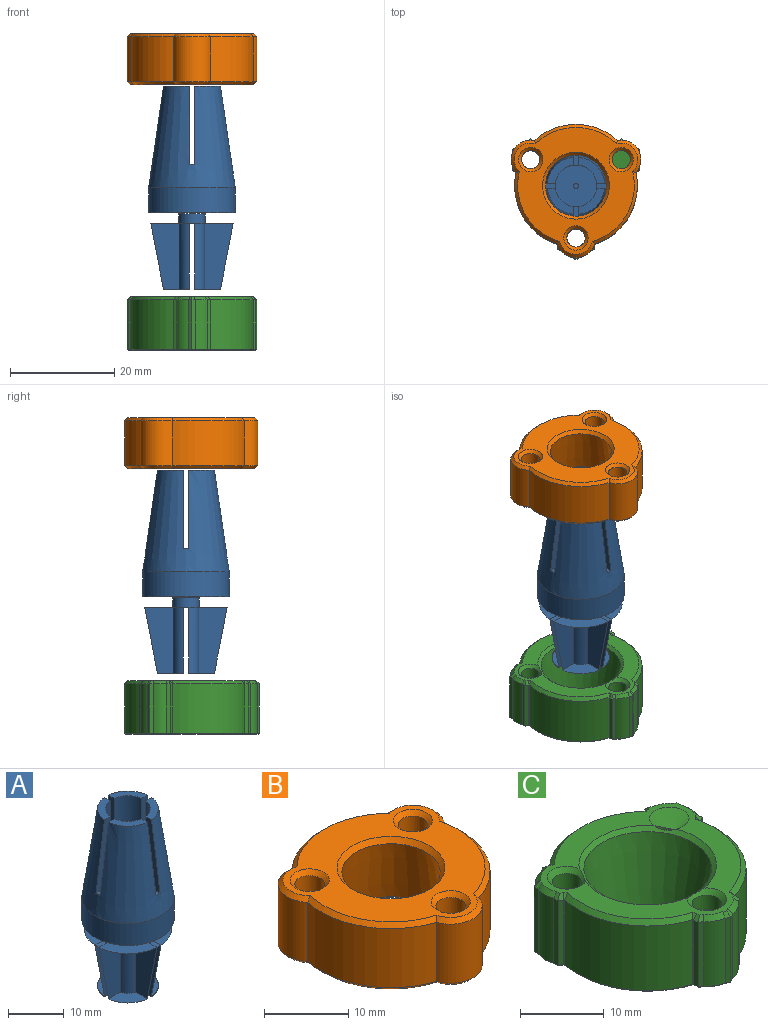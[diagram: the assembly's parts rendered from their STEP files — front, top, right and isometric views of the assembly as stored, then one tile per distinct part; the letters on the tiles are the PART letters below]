
ASSEMBLY  parts=3 mates=2
PART A: 40 faces, bbox 16.6x16.6x38.9 mm
  f0: plane 4.96x4.96mm, normal (0,0,-1), area 15.7mm2, adj f4,f5,f32,f38
  f1: plane 4.96x4.96mm, normal (0,0,-1), area 15.7mm2, adj f4,f5,f31,f35
  f2: plane 4.96x4.96mm, normal (0,0,-1), area 15.7mm2, adj f4,f5,f28,f37
  f3: plane 4.96x4.96mm, normal (0,0,-1), area 15.7mm2, adj f4,f5,f29,f34
  f4: cone r=8.3mm half-angle=10.9deg, axis (0,0,1), area 55.8mm2, adj f0,f1,f2,f3,f11,f28,f29,f30
  f5: cylinder r=2.5mm len=14.41mm, axis (0,0,-1), area 175.9mm2, adj f0,f1,f2,f3,f15,f28,f29,f30
  f6: cone r=5.48mm half-angle=8.2deg, axis (0,0,-1), area 789.9mm2, adj f7,f8,f9,f10,f11,f16,f17,f18
  f7: plane 4.96x4.96mm, normal (0,0,1), area 9.6mm2, adj f6,f12,f16,f25
  f8: plane 4.96x4.96mm, normal (0,0,1), area 9.6mm2, adj f6,f12,f17,f23
  f9: plane 4.96x4.96mm, normal (0,0,1), area 9.6mm2, adj f6,f12,f20,f26
  f10: plane 4.96x4.96mm, normal (0,0,1), area 9.6mm2, adj f6,f12,f19,f24
  f11: cylinder r=8.3mm len=16.6mm, axis (0,0,-1), area 249.6mm2, adj f4,f6
  f12: cylinder r=4mm len=19.47mm, axis (0,0,-1), area 429.1mm2, adj f7,f8,f9,f10,f13,f16,f17,f18
  f13: plane 8x8mm, normal (0,0,1), area 49.5mm2, adj f12,f14
  f14: cylinder r=0.5mm len=5mm, axis (0,0,-1), area 15.7mm2, adj f13,f15
  f15: plane 5x5mm, normal (0,0,-1), area 18.8mm2, adj f5,f14
  f16: plane 15.03x3.7mm, normal (0,1,0), area 38.7mm2, adj f6,f7,f12,f18
  f17: plane 15.03x3.7mm, normal (0,-1,0), area 38.7mm2, adj f6,f8,f12,f18
  f18: plane 3.69x1mm, normal (0,0,1), area 3.7mm2, adj f6,f12,f16,f17
  f19: plane 15.03x3.7mm, normal (0,-1,0), area 38.7mm2, adj f6,f10,f12,f21
  f20: plane 15.03x3.7mm, normal (0,1,0), area 38.7mm2, adj f6,f9,f12,f21
  f21: plane 3.69x1mm, normal (0,0,1), area 3.7mm2, adj f6,f12,f19,f20
  f22: plane 3.69x1mm, normal (0,0,1), area 3.7mm2, adj f6,f12,f23,f24
  f23: plane 15.03x3.7mm, normal (1,0,0), area 38.7mm2, adj f6,f8,f12,f22
  f24: plane 15.03x3.7mm, normal (-1,0,0), area 38.7mm2, adj f6,f10,f12,f22
  f25: plane 15.03x3.7mm, normal (1,0,0), area 38.7mm2, adj f6,f7,f12,f27
  f26: plane 15.03x3.7mm, normal (-1,0,0), area 38.7mm2, adj f6,f9,f12,f27
  f27: plane 3.69x1mm, normal (0,0,1), area 3.7mm2, adj f6,f12,f25,f26
  f28: plane 12.58x5.47mm, normal (-1,0,0), area 53mm2, adj f2,f4,f5,f30
  f29: plane 12.58x5.47mm, normal (1,0,0), area 53mm2, adj f3,f4,f5,f30
  f30: plane 5.45x1mm, normal (0,0,-1), area 5.4mm2, adj f4,f5,f28,f29
  f31: plane 12.58x5.47mm, normal (1,0,0), area 53mm2, adj f1,f4,f5,f33
  f32: plane 12.58x5.47mm, normal (-1,0,0), area 53mm2, adj f0,f4,f5,f33
  f33: plane 5.45x1mm, normal (0,0,-1), area 5.4mm2, adj f4,f5,f31,f32
  f34: plane 12.58x5.47mm, normal (0,1,0), area 53mm2, adj f3,f4,f5,f36
  f35: plane 12.58x5.47mm, normal (0,-1,0), area 53mm2, adj f1,f4,f5,f36
  f36: plane 5.45x1mm, normal (0,0,-1), area 5.4mm2, adj f4,f5,f34,f35
  f37: plane 12.58x5.47mm, normal (0,1,0), area 53mm2, adj f2,f4,f5,f39
  f38: plane 12.58x5.47mm, normal (0,-1,0), area 53mm2, adj f0,f4,f5,f39
  f39: plane 15.8x15.8mm, normal (0,0,-1), area 190.6mm2, adj f4,f5,f37,f38
PART B: 32 faces, bbox 24.8x25.5x9.7 mm
  f0: plane 24.34x23.67mm, normal (0,0,1), area 240.2mm2, adj f12,f13,f14,f15,f16,f17,f18,f19
  f1: cylinder r=11.75mm len=13.71mm, axis (0,0,-1), area 149.1mm2, adj f6,f10,f16,f26
  f2: cylinder r=11.75mm len=15.84mm, axis (0,0,-1), area 149.1mm2, adj f8,f10,f20,f30
  f3: plane 24.34x23.67mm, normal (0,0,-1), area 185.4mm2, adj f22,f23,f24,f25,f26,f27,f28,f29
  f4: cylinder r=11.75mm len=13.71mm, axis (0,0,-1), area 149.1mm2, adj f6,f8,f17,f27
  f5: cone r=7.14mm half-angle=8.2deg, axis (0,0,-1), area 351.4mm2, adj f21,f31
  f6: cylinder r=3.75mm len=8.58mm, axis (0,0,1), area 80.2mm2, adj f1,f4,f15,f25
  f7: cylinder r=1.75mm len=8.58mm, axis (0,0,1), area 94.3mm2, adj f14,f24
  f8: cylinder r=3.75mm len=8.58mm, axis (0,0,1), area 80.2mm2, adj f2,f4,f19,f29
  f9: cylinder r=1.75mm len=8.58mm, axis (0,0,1), area 94.3mm2, adj f13,f23
  f10: cylinder r=3.75mm len=8.58mm, axis (0,0,1), area 80.2mm2, adj f1,f2,f18,f28
  f11: cylinder r=1.75mm len=8.58mm, axis (0,0,1), area 94.3mm2, adj f12,f22
  f12: cone r=1.75mm half-angle=45deg, axis (0,0,1), area 10.5mm2, adj f0,f11
  f13: cone r=1.75mm half-angle=45deg, axis (0,0,1), area 10.5mm2, adj f0,f9
  f14: cone r=1.75mm half-angle=45deg, axis (0,0,1), area 10.5mm2, adj f0,f7
  f15: cone r=3.17mm half-angle=45deg, axis (0,0,-1), area 7.3mm2, adj f0,f6,f16,f17
  f16: cone r=11.75mm half-angle=45deg, axis (0,0,-1), area 14.1mm2, adj f0,f1,f15,f18
  f17: cone r=11.75mm half-angle=45deg, axis (0,0,-1), area 14.1mm2, adj f0,f4,f15,f19
  f18: cone r=3.17mm half-angle=45deg, axis (0,0,-1), area 7.3mm2, adj f0,f10,f16,f20
  f19: cone r=3.17mm half-angle=45deg, axis (0,0,-1), area 7.3mm2, adj f0,f8,f17,f20
  f20: cone r=11.75mm half-angle=45deg, axis (0,0,-1), area 14.1mm2, adj f0,f2,f18,f19
  f21: cone r=6.4mm half-angle=40.9deg, axis (0,0,1), area 33.6mm2, adj f0,f5
  f22: cone r=1.75mm half-angle=45deg, axis (0,0,-1), area 10.5mm2, adj f3,f11
  f23: cone r=1.75mm half-angle=45deg, axis (0,0,-1), area 10.5mm2, adj f3,f9
  f24: cone r=1.75mm half-angle=45deg, axis (0,0,-1), area 10.5mm2, adj f3,f7
  f25: cone r=3.17mm half-angle=45deg, axis (0,0,1), area 7.3mm2, adj f3,f6,f26,f27
  f26: cone r=11.17mm half-angle=45deg, axis (0,0,1), area 14.1mm2, adj f1,f3,f25,f28
  f27: cone r=11.17mm half-angle=45deg, axis (0,0,1), area 14.1mm2, adj f3,f4,f25,f29
  f28: cone r=3.17mm half-angle=45deg, axis (0,0,1), area 7.3mm2, adj f3,f10,f26,f30
  f29: cone r=3.17mm half-angle=45deg, axis (0,0,1), area 7.3mm2, adj f3,f8,f27,f30
  f30: cone r=11.17mm half-angle=45deg, axis (0,0,1), area 14.1mm2, adj f2,f3,f28,f29
  f31: cone r=7.07mm half-angle=49.1deg, axis (0,0,-1), area 35mm2, adj f3,f5
PART C: 155 faces, bbox 24.8x25.8x10.3 mm
  f0: cylinder r=1.75mm len=3.5mm, axis (0,0,-1), area 23.9mm2, adj f145,f152
  f1: cylinder r=1.75mm len=3.5mm, axis (0,0,-1), area 23.9mm2, adj f146,f154
  f2: cylinder r=1.75mm len=3.5mm, axis (0,0,-1), area 23.9mm2, adj f148,f150
  f3: plane 25.36x24.41mm, normal (0,0,-1), area 243.8mm2, adj f60,f61,f62,f63,f64,f65,f66,f67
  f4: cylinder r=3.75mm len=9.47mm, axis (0,0,-1), area 25.2mm2, adj f40,f45,f83,f122
  f5: cylinder r=3.75mm len=9.47mm, axis (0,0,-1), area 1.1mm2, adj f13,f42,f95,f134
  f6: cylinder r=3.75mm len=9.47mm, axis (0,0,-1), area 25.2mm2, adj f41,f43,f89,f128
  f7: cylinder r=3.75mm len=9.47mm, axis (0,0,-1), area 25.2mm2, adj f34,f39,f104,f144
  f8: cylinder r=3.75mm len=9.47mm, axis (0,0,-1), area 1.1mm2, adj f14,f36,f92,f133
  f9: cylinder r=3.75mm len=9.47mm, axis (0,0,-1), area 25.2mm2, adj f35,f37,f98,f139
  f10: cylinder r=3.75mm len=9.47mm, axis (0,0,-1), area 1.1mm2, adj f15,f25,f73,f112
  f11: cylinder r=3.75mm len=9.47mm, axis (0,0,-1), area 25.2mm2, adj f23,f26,f76,f117
  f12: cylinder r=3.75mm len=9.47mm, axis (0,0,-1), area 25.2mm2, adj f21,f24,f82,f123
  f13: cylinder r=11.75mm len=13.71mm, axis (0,0,-1), area 164.5mm2, adj f5,f20,f97,f136
  f14: cylinder r=11.75mm len=13.71mm, axis (0,0,-1), area 164.5mm2, adj f8,f19,f90,f131
  f15: cylinder r=11.75mm len=15.84mm, axis (0,0,-1), area 164.5mm2, adj f10,f18,f75,f114
  f16: plane 24.5x23.61mm, normal (0,0,1), area 157.5mm2, adj f112,f113,f114,f115,f116,f117,f118,f119
  f17: cone r=5.74mm half-angle=10.9deg, axis (0,0,1), area 409.3mm2, adj f111,f147
  f18: cylinder r=3.75mm len=9.47mm, axis (0,0,-1), area 1.1mm2, adj f15,f44,f77,f116
  f19: cylinder r=3.75mm len=9.47mm, axis (0,0,-1), area 1.1mm2, adj f14,f22,f88,f129
  f20: cylinder r=3.75mm len=9.47mm, axis (0,0,-1), area 1.1mm2, adj f13,f38,f99,f138
  f21: plane 9.47x0.73mm, normal (1,0,0), area 6.9mm2, adj f12,f22,f84,f125
  f22: plane 9.47x0.63mm, normal (0.5,-0.87,0), area 6.9mm2, adj f19,f21,f86,f127
  f23: plane 9.47x0.63mm, normal (0.5,0.87,0), area 6.9mm2, adj f11,f24,f78,f119
  f24: plane 9.47x0.73mm, normal (1,0,0), area 6.9mm2, adj f12,f23,f80,f121
  f25: plane 9.47x0.63mm, normal (-0.5,0.87,0), area 6.9mm2, adj f10,f26,f72,f113
  f26: plane 9.47x0.63mm, normal (0.5,0.87,0), area 6.9mm2, adj f11,f25,f74,f115
  f27: plane 2.8x2.29mm, normal (0.5,-0.87,0), area 7.4mm2, adj f28,f32,f33,f110
  f28: plane 2.8x2.29mm, normal (-0.5,-0.87,0), area 7.4mm2, adj f27,f29,f33,f108
  f29: plane 3.23x2.29mm, normal (-1,0,0), area 7.4mm2, adj f28,f30,f33,f106
  f30: plane 2.8x2.29mm, normal (-0.5,0.87,0), area 7.4mm2, adj f29,f31,f33,f105
  f31: plane 2.8x2.29mm, normal (0.5,0.87,0), area 7.4mm2, adj f30,f32,f33,f107
  f32: plane 3.23x2.29mm, normal (1,0,0), area 7.4mm2, adj f27,f31,f33,f109
  f33: plane 6.47x5.6mm, normal (0,0,-1), area 7.5mm2, adj f27,f28,f29,f30,f31,f32,f153
  f34: plane 9.47x0.63mm, normal (-0.5,-0.87,0), area 6.9mm2, adj f7,f35,f102,f143
  f35: plane 9.47x0.63mm, normal (0.5,-0.87,0), area 6.9mm2, adj f9,f34,f100,f141
  f36: plane 9.47x0.73mm, normal (1,0,0), area 6.9mm2, adj f8,f37,f94,f135
  f37: plane 9.47x0.63mm, normal (0.5,-0.87,0), area 6.9mm2, adj f9,f36,f96,f137
  f38: plane 9.47x0.73mm, normal (-1,0,0), area 6.9mm2, adj f20,f39,f101,f140
  f39: plane 9.47x0.63mm, normal (-0.5,-0.87,0), area 6.9mm2, adj f7,f38,f103,f142
  f40: plane 9.47x0.63mm, normal (-0.5,0.87,0), area 6.9mm2, adj f4,f41,f85,f124
  f41: plane 9.47x0.73mm, normal (-1,0,0), area 6.9mm2, adj f6,f40,f87,f126
  f42: plane 9.47x0.63mm, normal (-0.5,-0.87,0), area 6.9mm2, adj f5,f43,f93,f132
  f43: plane 9.47x0.73mm, normal (-1,0,0), area 6.9mm2, adj f6,f42,f91,f130
  f44: plane 9.47x0.63mm, normal (0.5,0.87,0), area 6.9mm2, adj f18,f45,f79,f118
  f45: plane 9.47x0.63mm, normal (-0.5,0.87,0), area 6.9mm2, adj f4,f44,f81,f120
  f46: plane 2.8x2.29mm, normal (0.5,-0.87,0), area 7.4mm2, adj f47,f51,f52,f65
  f47: plane 2.8x2.29mm, normal (-0.5,-0.87,0), area 7.4mm2, adj f46,f48,f52,f63
  f48: plane 3.23x2.29mm, normal (-1,0,0), area 7.4mm2, adj f47,f49,f52,f61
  f49: plane 2.8x2.29mm, normal (-0.5,0.87,0), area 7.4mm2, adj f48,f50,f52,f60
  f50: plane 2.8x2.29mm, normal (0.5,0.87,0), area 7.4mm2, adj f49,f51,f52,f62
  f51: plane 3.23x2.29mm, normal (1,0,0), area 7.4mm2, adj f46,f50,f52,f64
  f52: plane 6.47x5.6mm, normal (0,0,-1), area 7.5mm2, adj f46,f47,f48,f49,f50,f51,f151
  f53: plane 2.8x2.29mm, normal (0.5,0.87,0), area 7.4mm2, adj f54,f58,f59,f71
  f54: plane 3.23x2.29mm, normal (1,0,0), area 7.4mm2, adj f53,f55,f59,f69
  f55: plane 2.8x2.29mm, normal (0.5,-0.87,0), area 7.4mm2, adj f54,f56,f59,f67
  f56: plane 2.8x2.29mm, normal (-0.5,-0.87,0), area 7.4mm2, adj f55,f57,f59,f66
  f57: plane 3.23x2.29mm, normal (-1,0,0), area 7.4mm2, adj f56,f58,f59,f68
  f58: plane 2.8x2.29mm, normal (-0.5,0.87,0), area 7.4mm2, adj f53,f57,f59,f70
  f59: plane 6.47x5.6mm, normal (0,0,-1), area 7.5mm2, adj f53,f54,f55,f56,f57,f58,f149
  f60: plane 3.01x1.86mm, normal (-0.35,0.61,-0.71), area 1mm2, adj f3,f49,f61,f62
  f61: plane 3.47x0.21mm, normal (-0.71,0,-0.71), area 1mm2, adj f3,f48,f60,f63
  f62: plane 3.01x1.86mm, normal (0.35,0.61,-0.71), area 1mm2, adj f3,f50,f60,f64
  f63: plane 3.01x1.86mm, normal (-0.35,-0.61,-0.71), area 1mm2, adj f3,f47,f61,f65
  f64: plane 3.47x0.21mm, normal (0.71,0,-0.71), area 1mm2, adj f3,f51,f62,f65
  f65: plane 3.01x1.86mm, normal (0.35,-0.61,-0.71), area 1mm2, adj f3,f46,f63,f64
  f66: plane 3.01x1.86mm, normal (-0.35,-0.61,-0.71), area 1mm2, adj f3,f56,f67,f68
  f67: plane 3.01x1.86mm, normal (0.35,-0.61,-0.71), area 1mm2, adj f3,f55,f66,f69
  f68: plane 3.47x0.21mm, normal (-0.71,0,-0.71), area 1mm2, adj f3,f57,f66,f70
  f69: plane 3.47x0.21mm, normal (0.71,0,-0.71), area 1mm2, adj f3,f54,f67,f71
  f70: plane 3.01x1.86mm, normal (-0.35,0.61,-0.71), area 1mm2, adj f3,f58,f68,f71
  f71: plane 3.01x1.86mm, normal (0.35,0.61,-0.71), area 1mm2, adj f3,f53,f69,f70
  f72: plane 0.63x0.56mm, normal (-0.35,0.61,-0.71), area 0.2mm2, adj f3,f25,f73,f74
  f73: cone r=3.54mm half-angle=45deg, axis (0,0,1), area 0.1mm2, adj f3,f10,f72,f75
  f74: plane 0.63x0.56mm, normal (0.35,0.61,-0.71), area 0.2mm2, adj f3,f26,f72,f76
  f75: cone r=11.54mm half-angle=45deg, axis (0,0,1), area 5.1mm2, adj f3,f15,f73,f77
  f76: cone r=3.54mm half-angle=45deg, axis (0,0,1), area 0.8mm2, adj f3,f11,f74,f78
  f77: cone r=3.54mm half-angle=45deg, axis (0,0,1), area 0.1mm2, adj f3,f18,f75,f79
  f78: plane 0.76x0.48mm, normal (0.35,0.61,-0.71), area 0.2mm2, adj f3,f23,f76,f80
  f79: plane 0.63x0.56mm, normal (0.35,0.61,-0.71), area 0.2mm2, adj f3,f44,f77,f81
  f80: plane 0.76x0.21mm, normal (0.71,0,-0.71), area 0.2mm2, adj f3,f24,f78,f82
  f81: plane 0.63x0.56mm, normal (-0.35,0.61,-0.71), area 0.2mm2, adj f3,f45,f79,f83
  f82: cone r=3.54mm half-angle=45deg, axis (0,0,1), area 0.8mm2, adj f3,f12,f80,f84
  f83: cone r=3.54mm half-angle=45deg, axis (0,0,1), area 0.8mm2, adj f3,f4,f81,f85
  f84: plane 0.76x0.21mm, normal (0.71,0,-0.71), area 0.2mm2, adj f3,f21,f82,f86
  f85: plane 0.76x0.48mm, normal (-0.35,0.61,-0.71), area 0.2mm2, adj f3,f40,f83,f87
  f86: plane 0.76x0.48mm, normal (0.35,-0.61,-0.71), area 0.2mm2, adj f3,f22,f84,f88
  f87: plane 0.76x0.21mm, normal (-0.71,0,-0.71), area 0.2mm2, adj f3,f41,f85,f89
  f88: cone r=3.54mm half-angle=45deg, axis (0,0,1), area 0.1mm2, adj f3,f19,f86,f90
  f89: cone r=3.54mm half-angle=45deg, axis (0,0,1), area 0.8mm2, adj f3,f6,f87,f91
  f90: cone r=11.54mm half-angle=45deg, axis (0,0,1), area 5.1mm2, adj f3,f14,f88,f92
  f91: plane 0.76x0.21mm, normal (-0.71,0,-0.71), area 0.2mm2, adj f3,f43,f89,f93
  f92: cone r=3.54mm half-angle=45deg, axis (0,0,1), area 0.1mm2, adj f3,f8,f90,f94
  f93: plane 0.76x0.48mm, normal (-0.35,-0.61,-0.71), area 0.2mm2, adj f3,f42,f91,f95
  f94: plane 0.76x0.21mm, normal (0.71,0,-0.71), area 0.2mm2, adj f3,f36,f92,f96
  f95: cone r=3.54mm half-angle=45deg, axis (0,0,1), area 0.1mm2, adj f3,f5,f93,f97
  f96: plane 0.76x0.48mm, normal (0.35,-0.61,-0.71), area 0.2mm2, adj f3,f37,f94,f98
  f97: cone r=11.54mm half-angle=45deg, axis (0,0,1), area 5.1mm2, adj f3,f13,f95,f99
  f98: cone r=3.54mm half-angle=45deg, axis (0,0,1), area 0.8mm2, adj f3,f9,f96,f100
  f99: cone r=3.54mm half-angle=45deg, axis (0,0,1), area 0.1mm2, adj f3,f20,f97,f101
  f100: plane 0.63x0.56mm, normal (0.35,-0.61,-0.71), area 0.2mm2, adj f3,f35,f98,f102
  f101: plane 0.76x0.21mm, normal (-0.71,0,-0.71), area 0.2mm2, adj f3,f38,f99,f103
  f102: plane 0.63x0.56mm, normal (-0.35,-0.61,-0.71), area 0.2mm2, adj f3,f34,f100,f104
  f103: plane 0.76x0.48mm, normal (-0.35,-0.61,-0.71), area 0.2mm2, adj f3,f39,f101,f104
  f104: cone r=3.54mm half-angle=45deg, axis (0,0,1), area 0.8mm2, adj f3,f7,f102,f103
  f105: plane 3.01x1.86mm, normal (-0.35,0.61,-0.71), area 1mm2, adj f3,f30,f106,f107
  f106: plane 3.47x0.21mm, normal (-0.71,0,-0.71), area 1mm2, adj f3,f29,f105,f108
  f107: plane 3.01x1.86mm, normal (0.35,0.61,-0.71), area 1mm2, adj f3,f31,f105,f109
  f108: plane 3.01x1.86mm, normal (-0.35,-0.61,-0.71), area 1mm2, adj f3,f28,f106,f110
  f109: plane 3.47x0.21mm, normal (0.71,0,-0.71), area 1mm2, adj f3,f32,f107,f110
  f110: plane 3.01x1.86mm, normal (0.35,-0.61,-0.71), area 1mm2, adj f3,f27,f108,f109
  f111: cone r=5.78mm half-angle=39.5deg, axis (0,0,-1), area 11.8mm2, adj f3,f17
  f112: cone r=3.14mm half-angle=45deg, axis (0,0,-1), area 0.3mm2, adj f10,f16,f113,f114
  f113: plane 0.95x0.64mm, normal (-0.35,0.61,0.71), area 0.5mm2, adj f16,f25,f112,f115
  f114: cone r=11.75mm half-angle=45deg, axis (0,0,-1), area 14.8mm2, adj f15,f16,f112,f116
  f115: plane 0.95x0.64mm, normal (0.35,0.61,0.71), area 0.5mm2, adj f16,f26,f113,f117
  f116: cone r=3.14mm half-angle=45deg, axis (0,0,-1), area 0.3mm2, adj f16,f18,f114,f118
  f117: cone r=3.14mm half-angle=45deg, axis (0,0,-1), area 2.2mm2, adj f11,f16,f115,f119
  f118: plane 0.95x0.64mm, normal (0.35,0.61,0.71), area 0.5mm2, adj f16,f44,f116,f120
  f119: plane 1.04x0.72mm, normal (0.35,0.61,0.71), area 0.5mm2, adj f16,f23,f117,f121
  f120: plane 0.95x0.64mm, normal (-0.35,0.61,0.71), area 0.5mm2, adj f16,f45,f118,f122
  f121: plane 0.85x0.61mm, normal (0.71,0,0.71), area 0.5mm2, adj f16,f24,f119,f123
  f122: cone r=3.14mm half-angle=45deg, axis (0,0,-1), area 2.2mm2, adj f4,f16,f120,f124
  f123: cone r=3.14mm half-angle=45deg, axis (0,0,-1), area 2.2mm2, adj f12,f16,f121,f125
  f124: plane 1.04x0.72mm, normal (-0.35,0.61,0.71), area 0.5mm2, adj f16,f40,f122,f126
  f125: plane 0.85x0.61mm, normal (0.71,0,0.71), area 0.5mm2, adj f16,f21,f123,f127
  f126: plane 0.85x0.61mm, normal (-0.71,0,0.71), area 0.5mm2, adj f16,f41,f124,f128
  f127: plane 1.04x0.72mm, normal (0.35,-0.61,0.71), area 0.5mm2, adj f16,f22,f125,f129
  f128: cone r=3.14mm half-angle=45deg, axis (0,0,-1), area 2.2mm2, adj f6,f16,f126,f130
  f129: cone r=3.14mm half-angle=45deg, axis (0,0,-1), area 0.3mm2, adj f16,f19,f127,f131
  f130: plane 0.85x0.61mm, normal (-0.71,0,0.71), area 0.5mm2, adj f16,f43,f128,f132
  f131: cone r=11.75mm half-angle=45deg, axis (0,0,-1), area 14.8mm2, adj f14,f16,f129,f133
  f132: plane 1.04x0.72mm, normal (-0.35,-0.61,0.71), area 0.5mm2, adj f16,f42,f130,f134
  f133: cone r=3.14mm half-angle=45deg, axis (0,0,-1), area 0.3mm2, adj f8,f16,f131,f135
  f134: cone r=3.14mm half-angle=45deg, axis (0,0,-1), area 0.3mm2, adj f5,f16,f132,f136
  f135: plane 0.85x0.61mm, normal (0.71,0,0.71), area 0.5mm2, adj f16,f36,f133,f137
  f136: cone r=11.75mm half-angle=45deg, axis (0,0,-1), area 14.8mm2, adj f13,f16,f134,f138
  f137: plane 1.04x0.72mm, normal (0.35,-0.61,0.71), area 0.5mm2, adj f16,f37,f135,f139
  f138: cone r=3.14mm half-angle=45deg, axis (0,0,-1), area 0.3mm2, adj f16,f20,f136,f140
  f139: cone r=3.14mm half-angle=45deg, axis (0,0,-1), area 2.2mm2, adj f9,f16,f137,f141
  f140: plane 0.85x0.61mm, normal (-0.71,0,0.71), area 0.5mm2, adj f16,f38,f138,f142
  f141: plane 0.95x0.64mm, normal (0.35,-0.61,0.71), area 0.5mm2, adj f16,f35,f139,f143
  f142: plane 1.04x0.72mm, normal (-0.35,-0.61,0.71), area 0.5mm2, adj f16,f39,f140,f144
  f143: plane 0.95x0.64mm, normal (-0.35,-0.61,0.71), area 0.5mm2, adj f16,f34,f141,f144
  f144: cone r=3.14mm half-angle=45deg, axis (0,0,-1), area 2.2mm2, adj f7,f16,f142,f143
  f145: cone r=1.75mm half-angle=45deg, axis (0,0,1), area 10.3mm2, adj f0,f16,f147
  f146: cone r=1.75mm half-angle=45deg, axis (0,0,1), area 10.3mm2, adj f1,f16,f147
  f147: cone r=8.22mm half-angle=50.5deg, axis (0,0,1), area 36.1mm2, adj f16,f17,f145,f146,f148
  f148: cone r=1.75mm half-angle=45deg, axis (0,0,1), area 10.3mm2, adj f2,f16,f147
  f149: cylinder r=2.5mm len=5mm, axis (0,0,-1), area 78.5mm2, adj f59,f150
  f150: plane 5x5mm, normal (0,0,-1), area 10mm2, adj f2,f149
  f151: cylinder r=2.5mm len=5mm, axis (0,0,-1), area 78.5mm2, adj f52,f152
  f152: plane 5x5mm, normal (0,0,-1), area 10mm2, adj f0,f151
  f153: cylinder r=2.5mm len=5mm, axis (0,0,-1), area 78.5mm2, adj f33,f154
  f154: plane 5x5mm, normal (0,0,-1), area 10mm2, adj f1,f153
PLACE A t=(-15.15,-32.72,1.53)mm
PLACE B t=(-15.15,-32.72,11.56)mm
PLACE C t=(-15.15,-32.72,-10.19)mm
MATE slider B.f1 <-> A.f4  axis (0,0,1) through (-15.15,-28.06,23.24)mm
MATE slider C.f13 <-> A.f4  axis (0,0,-1) through (-15.15,-28.06,-37.39)mm
